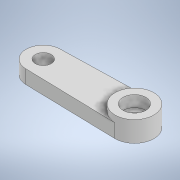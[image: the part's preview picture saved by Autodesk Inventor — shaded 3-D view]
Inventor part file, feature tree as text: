
AUTODESK INVENTOR PART (.ipt)
format: ipt  version: 2021 (Build 250183000, 183)  size: 140,800 bytes
history: native  units: mm
features: extrude x5, sketch x5
ambient origin geometry x8: Origin, YZ Plane, XZ Plane, XY Plane, X Axis, Y Axis, Z Axis, Center Point
bodies: Solid1 (feature_tree)
feature tree (10):
  extrude  "Extrusion1"  Depth=10.0mm
  extrude  "Extrusion2"  Depth=10.0mm
  extrude  "Extrusion3"  Depth=3.0mm
  extrude  "Extrusion4"  Depth=1.5mm
  extrude  "Extrusion5"  Depth=2.5mm
  sketch  "Sketch1"  dims[d0=10.0mm d1=7.5mm]
  sketch  "Sketch2"  dims[d2=3.5mm d3=10.0mm]
  sketch  "Sketch4"  dims[d7=3.0mm d8=0.0mm d9=5.0mm]
  sketch  "Sketch5"  dims[d11=1.5mm d12=0.0mm d13=5.0mm]
  sketch  "Sketch6"  dims[d14=1.0mm d15=0.0mm d16=2.5mm d17=0.8mm d18=0.0mm d19=5.0mm d20=1.2mm d21=0.0mm d10=0.872665mm]
